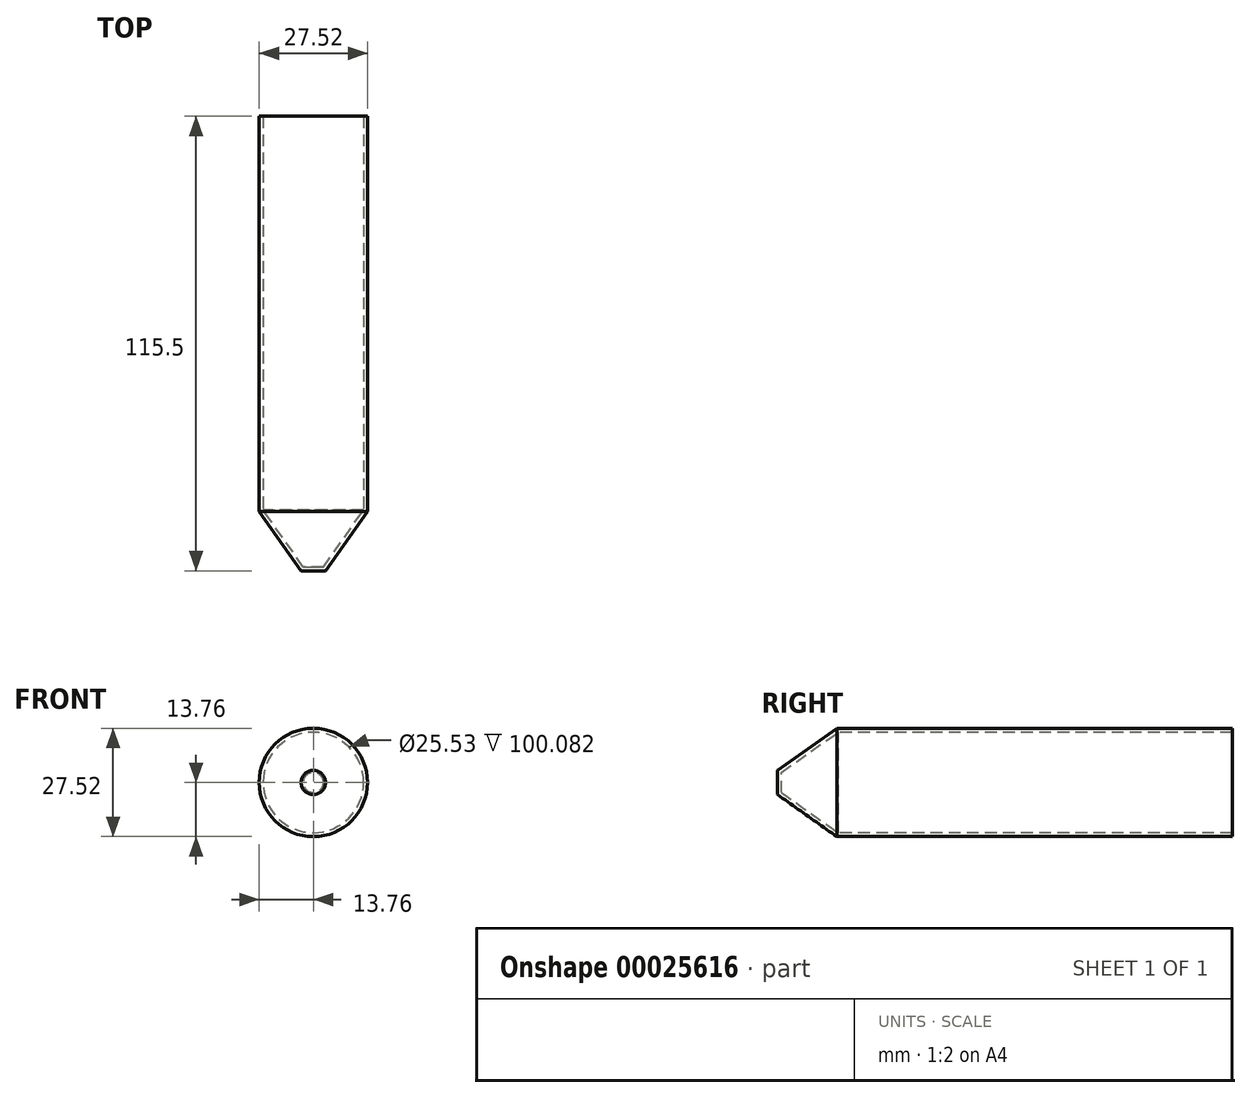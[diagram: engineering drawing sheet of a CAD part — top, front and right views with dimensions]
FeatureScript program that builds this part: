
annotation { "Feature Type Name" : "Feature", "Feature Type Description" : "" }
export const myFeature = defineFeature(function(context is Context, id is Id, definition is map)
    precondition{}
    {
        {
            var Q0;
            Q0=qCreatedBy(makeId("Top.planeOp"),FACE);
            var sketch = newSketch(context, id + "F0", { "sketchPlane" : qUnion([Q0])});
            skLineSegment(sketch, "E0", {"start": v(0, 0) * mm, "end": v(3.08, 0) * mm});
            skLineSegment(sketch, "E1", {"start": v(3.07, 0) * mm, "end": v(13.76, 15.1) * mm});
            skLineSegment(sketch, "E2", {"start": v(13.76, 15.1) * mm, "end": v(13.76, 115.5) * mm});
            skLineSegment(sketch, "E3", {"start": v(3.08, 0) * mm, "end": v(13.76, 0) * mm, "construction": true});
            skLineSegment(sketch, "E4.0", {"start": v(12.76, 15.42) * mm, "end": v(12.76, 115.5) * mm});
            skLineSegment(sketch, "E4.1", {"start": v(2.56, 1) * mm, "end": v(12.76, 15.42) * mm});
            skLineSegment(sketch, "E4.2", {"start": v(0, 1) * mm, "end": v(2.56, 1) * mm});
            skLineSegment(sketch, "E5", {"start": v(0, 0) * mm, "end": v(0, 1) * mm});
            skLineSegment(sketch, "E6", {"start": v(12.76, 115.5) * mm, "end": v(13.76, 115.5) * mm});
            skSolve(sketch);
        }
        {
            var Q0;
            Q0 = qSketchRegion(id + "F0", true);
            var Q1;
            Q1=sQuery(id+"F0.wireOp",EDGE,"E5");
            revolve(context, id + "F1", {"entities" : qUnion([Q0]), "axis" : qUnion([Q1]), "revolveType" : RevolveType.FULL});
        }
    });
